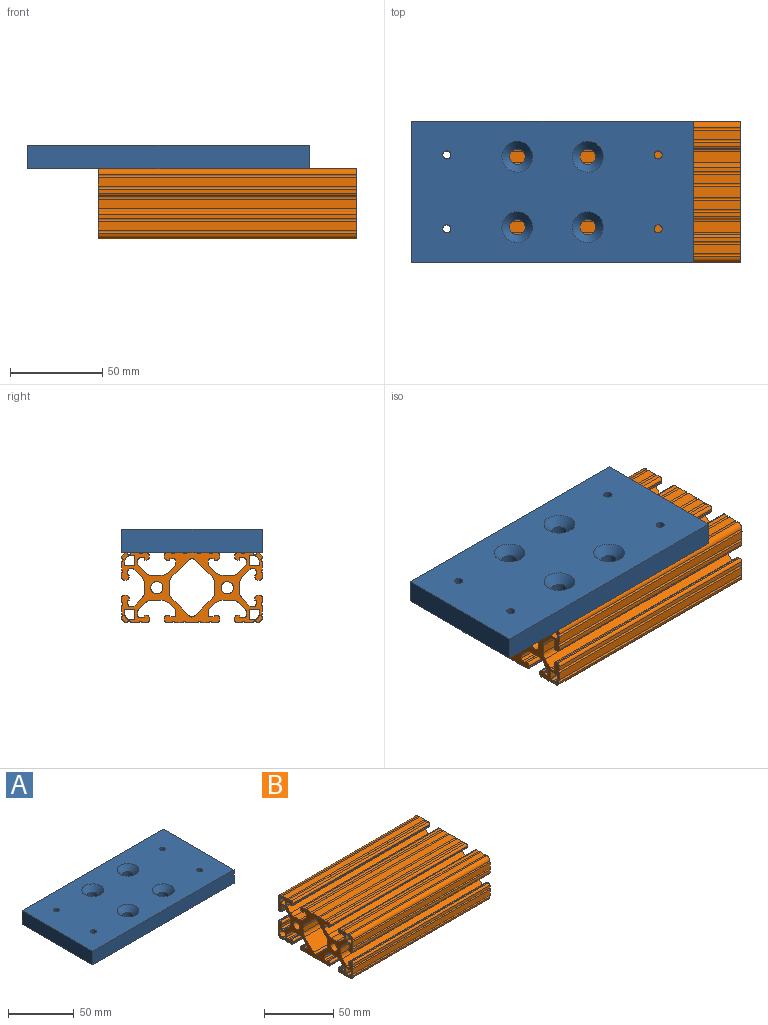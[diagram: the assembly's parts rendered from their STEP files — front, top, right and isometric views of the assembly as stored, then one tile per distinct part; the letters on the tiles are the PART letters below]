
ASSEMBLY  parts=2 mates=2
PART A: 22 faces, bbox 152.4x76.2x12.7 mm
  f0: plane 76.2x12.7mm, normal (1,0,0), area 967.7mm2, adj f1,f3,f4,f5
  f1: plane 152.4x12.7mm, normal (0,1,0), area 1935.5mm2, adj f0,f2,f4,f5
  f2: plane 76.2x12.7mm, normal (-1,0,0), area 967.7mm2, adj f1,f3,f4,f5
  f3: plane 152.4x12.7mm, normal (0,-1,0), area 1935.5mm2, adj f0,f2,f4,f5
  f4: plane 152.4x76.2mm, normal (0,0,1), area 10679.8mm2, adj f0,f1,f2,f3,f7,f9,f11,f13
  f5: plane 152.4x76.2mm, normal (0,0,-1), area 11137.3mm2, adj f0,f1,f2,f3,f6,f8,f10,f12
  f6: cylinder r=4.22mm len=8.43mm, axis (0,0,1), area 211.1mm2, adj f5,f7
  f7: cone r=4.22mm half-angle=41deg, axis (0,0,1), area 247.2mm2, adj f4,f6
  f8: cylinder r=4.22mm len=8.43mm, axis (0,0,1), area 211.1mm2, adj f5,f9
  f9: cone r=4.22mm half-angle=41deg, axis (0,0,1), area 247.2mm2, adj f4,f8
  f10: cylinder r=4.22mm len=8.43mm, axis (0,0,1), area 211.1mm2, adj f5,f11
  f11: cone r=4.22mm half-angle=41deg, axis (0,0,1), area 247.2mm2, adj f4,f10
  f12: cylinder r=4.22mm len=8.43mm, axis (0,0,1), area 211.1mm2, adj f5,f13
  f13: cone r=4.22mm half-angle=41deg, axis (0,0,1), area 247.2mm2, adj f4,f12
  f14: cylinder r=2.2mm len=10.42mm, axis (0,0,-1), area 144mm2, adj f4,f15
  f15: cone r=2.2mm half-angle=45deg, axis (0,0,-1), area 67.7mm2, adj f5,f14
  f16: cylinder r=2.2mm len=10.42mm, axis (0,0,-1), area 144mm2, adj f4,f17
  f17: cone r=2.2mm half-angle=45deg, axis (0,0,-1), area 67.7mm2, adj f5,f16
  f18: cylinder r=2.2mm len=10.42mm, axis (0,0,-1), area 144mm2, adj f4,f19
  f19: cone r=2.2mm half-angle=45deg, axis (0,0,-1), area 67.7mm2, adj f5,f18
  f20: cylinder r=2.2mm len=10.42mm, axis (0,0,-1), area 144mm2, adj f4,f21
  f21: cone r=2.2mm half-angle=45deg, axis (0,0,-1), area 67.7mm2, adj f5,f20
PART B: 266 faces, bbox 139.7x76.2x38.1 mm
  f0: cylinder r=0.76mm len=139.7mm, axis (-1,0,0), area 334.4mm2, adj f1,f263,f264,f265
  f1: plane 139.7x6.25mm, normal (0,0,1), area 872.8mm2, adj f0,f2,f264,f265
  f2: cylinder r=0.76mm len=139.7mm, axis (-1,0,0), area 334.4mm2, adj f1,f3,f264,f265
  f3: plane 139.7x4.83mm, normal (0,0,1), area 674.3mm2, adj f2,f4,f264,f265
  f4: cylinder r=0.76mm len=139.7mm, axis (-1,0,0), area 334.4mm2, adj f3,f5,f264,f265
  f5: plane 139.7x2.41mm, normal (0,0,1), area 337.1mm2, adj f4,f6,f264,f265
  f6: cylinder r=1.57mm len=139.7mm, axis (-1,0,0), area 345.6mm2, adj f5,f7,f264,f265
  f7: plane 139.7x0.91mm, normal (0,-1,0), area 127.7mm2, adj f6,f8,f264,f265
  f8: cylinder r=1.57mm len=139.7mm, axis (-1,0,0), area 345.6mm2, adj f7,f9,f264,f265
  f9: plane 139.7x0.94mm, normal (0,0,-1), area 131.4mm2, adj f8,f10,f264,f265
  f10: cylinder r=0.25mm len=139.7mm, axis (-1,0,0), area 55.7mm2, adj f9,f11,f264,f265
  f11: plane 139.7x0.26mm, normal (0,1,0), area 36.1mm2, adj f10,f12,f264,f265
  f12: cylinder r=0.25mm len=139.7mm, axis (-1,0,0), area 55.7mm2, adj f11,f13,f264,f265
  f13: plane 139.7x1.93mm, normal (0,0,-1), area 269.6mm2, adj f12,f14,f264,f265
  f14: cylinder r=1.27mm len=139.7mm, axis (-1,0,0), area 278.7mm2, adj f13,f15,f264,f265
  f15: plane 139.7x1.85mm, normal (0,-1,0), area 258.2mm2, adj f14,f16,f264,f265
  f16: cylinder r=0.89mm len=139.7mm, axis (-1,0,0), area 97.5mm2, adj f15,f17,f264,f265
  f17: plane 139.7x3.88mm, normal (0,-0.71,0.71), area 766.8mm2, adj f16,f18,f264,f265
  f18: cylinder r=4.67mm len=139.7mm, axis (-1,0,0), area 512.4mm2, adj f17,f19,f264,f265
  f19: plane 139.7x5.73mm, normal (0,0,1), area 800.9mm2, adj f18,f20,f264,f265
  f20: cylinder r=4.56mm len=139.7mm, axis (-1,0,0), area 499.9mm2, adj f19,f21,f264,f265
  f21: plane 139.7x3.8mm, normal (0,0.71,0.71), area 750.9mm2, adj f20,f22,f264,f265
  f22: cylinder r=1.28mm len=139.7mm, axis (-1,0,0), area 140.3mm2, adj f21,f23,f264,f265
  f23: plane 139.7x2.15mm, normal (0,1,0), area 300.9mm2, adj f22,f24,f264,f265
  f24: cylinder r=1.27mm len=139.7mm, axis (-1,0,0), area 278.7mm2, adj f23,f25,f264,f265
  f25: plane 139.7x1.93mm, normal (0,0,-1), area 269.6mm2, adj f24,f26,f264,f265
  f26: cylinder r=0.25mm len=139.7mm, axis (-1,0,0), area 55.7mm2, adj f25,f27,f264,f265
  f27: plane 139.7x0.73mm, normal (0,-1,0), area 101.4mm2, adj f26,f28,f264,f265
  f28: cylinder r=0.25mm len=139.7mm, axis (-1,0,0), area 55.7mm2, adj f27,f29,f264,f265
  f29: plane 139.7x0.94mm, normal (0,0,-1), area 131.4mm2, adj f28,f30,f264,f265
  f30: cylinder r=1.57mm len=139.7mm, axis (-1,0,0), area 345.6mm2, adj f29,f31,f264,f265
  f31: plane 139.7x0.89mm, normal (0,1,0), area 124.4mm2, adj f30,f32,f264,f265
  f32: cylinder r=1.6mm len=139.7mm, axis (-1,0,0), area 350.8mm2, adj f31,f33,f264,f265
  f33: plane 139.7x2.23mm, normal (0,0,1), area 312.1mm2, adj f32,f34,f264,f265
  f34: cylinder r=0.76mm len=139.7mm, axis (-1,0,0), area 334.4mm2, adj f33,f35,f264,f265
  f35: plane 139.7x4.93mm, normal (0,0,1), area 688.7mm2, adj f34,f36,f264,f265
  f36: cylinder r=0.81mm len=139.7mm, axis (-1,0,0), area 447.7mm2, adj f35,f37,f264,f265
  f37: cylinder r=3.17mm len=139.7mm, axis (-1,0,0), area 701.7mm2, adj f36,f38,f264,f265
  f38: cylinder r=0.76mm len=139.7mm, axis (-1,0,0), area 334.8mm2, adj f37,f39,f264,f265
  f39: plane 139.7x4.83mm, normal (0,-1,0), area 674.5mm2, adj f38,f40,f264,f265
  f40: cylinder r=0.76mm len=139.7mm, axis (-1,0,0), area 334.4mm2, adj f39,f41,f264,f265
  f41: plane 139.7x2.33mm, normal (0,-1,0), area 325.1mm2, adj f40,f42,f264,f265
  f42: cylinder r=1.53mm len=139.7mm, axis (-1,0,0), area 336.4mm2, adj f41,f43,f264,f265
  f43: plane 139.7x0.96mm, normal (0,0,-1), area 133.6mm2, adj f42,f44,f264,f265
  f44: cylinder r=1.57mm len=139.7mm, axis (-1,0,0), area 345.6mm2, adj f43,f45,f264,f265
  f45: plane 139.7x1.02mm, normal (0,1,0), area 142.2mm2, adj f44,f46,f264,f265
  f46: cylinder r=0.25mm len=139.7mm, axis (-1,0,0), area 55.7mm2, adj f45,f47,f264,f265
  f47: plane 139.7x0.1mm, normal (0,0,1), area 14.4mm2, adj f46,f48,f264,f265
  f48: cylinder r=0.25mm len=139.7mm, axis (-1,0,0), area 55.7mm2, adj f47,f49,f264,f265
  f49: plane 139.7x1.81mm, normal (0,1,0), area 253.5mm2, adj f48,f50,f264,f265
  f50: cylinder r=1.26mm len=139.7mm, axis (-1,0,0), area 277.4mm2, adj f49,f51,f264,f265
  f51: plane 139.7x1.35mm, normal (0,0,-1), area 188.5mm2, adj f50,f52,f264,f265
  f52: cylinder r=0.87mm len=139.7mm, axis (-1,0,0), area 95.3mm2, adj f51,f53,f264,f265
  f53: plane 139.7x4.22mm, normal (0,-0.71,-0.71), area 834mm2, adj f52,f54,f264,f265
  f54: cylinder r=4.75mm len=139.7mm, axis (-1,0,0), area 521.2mm2, adj f53,f55,f264,f265
  f55: plane 139.7x4.92mm, normal (0,-1,0), area 686.6mm2, adj f54,f56,f264,f265
  f56: cylinder r=4.75mm len=139.7mm, axis (-1,0,0), area 521.2mm2, adj f55,f57,f264,f265
  f57: plane 139.7x4.22mm, normal (0,-0.71,0.71), area 834mm2, adj f56,f58,f264,f265
  f58: cylinder r=0.87mm len=139.7mm, axis (-1,0,0), area 95.3mm2, adj f57,f59,f264,f265
  f59: plane 139.7x1.35mm, normal (0,0,1), area 188.5mm2, adj f58,f60,f264,f265
  f60: cylinder r=1.26mm len=139.7mm, axis (-1,0,0), area 277.4mm2, adj f59,f61,f264,f265
  f61: plane 139.7x1.81mm, normal (0,1,0), area 253.5mm2, adj f60,f62,f264,f265
  f62: cylinder r=0.25mm len=139.7mm, axis (-1,0,0), area 55.7mm2, adj f61,f63,f264,f265
  f63: plane 139.7x0.1mm, normal (0,0,-1), area 14.4mm2, adj f62,f64,f264,f265
  f64: cylinder r=0.25mm len=139.7mm, axis (-1,0,0), area 55.7mm2, adj f63,f65,f264,f265
  f65: plane 139.7x1.02mm, normal (0,1,0), area 142.2mm2, adj f64,f66,f264,f265
  f66: cylinder r=1.57mm len=139.7mm, axis (-1,0,0), area 345.6mm2, adj f65,f67,f264,f265
  f67: plane 139.7x0.96mm, normal (0,0,1), area 133.6mm2, adj f66,f68,f264,f265
  f68: cylinder r=1.53mm len=139.7mm, axis (-1,0,0), area 336.4mm2, adj f67,f69,f264,f265
  f69: plane 139.7x2.33mm, normal (0,-1,0), area 325.1mm2, adj f68,f70,f264,f265
  f70: cylinder r=0.76mm len=139.7mm, axis (-1,0,0), area 334.4mm2, adj f69,f71,f264,f265
  f71: plane 139.7x4.83mm, normal (0,-1,0), area 674.5mm2, adj f70,f72,f264,f265
  f72: cylinder r=0.76mm len=139.7mm, axis (-1,0,0), area 334.8mm2, adj f71,f73,f264,f265
  f73: cylinder r=3.17mm len=139.7mm, axis (-1,0,0), area 701.7mm2, adj f72,f74,f264,f265
  f74: cylinder r=0.81mm len=139.7mm, axis (-1,0,0), area 447.7mm2, adj f73,f75,f264,f265
  f75: plane 139.7x4.93mm, normal (0,0,-1), area 688.7mm2, adj f74,f76,f264,f265
  f76: cylinder r=0.76mm len=139.7mm, axis (-1,0,0), area 334.4mm2, adj f75,f77,f264,f265
  f77: plane 139.7x2.23mm, normal (0,0,-1), area 312.1mm2, adj f76,f78,f264,f265
  f78: cylinder r=1.6mm len=139.7mm, axis (-1,0,0), area 350.8mm2, adj f77,f79,f264,f265
  f79: plane 139.7x0.89mm, normal (0,1,0), area 124.4mm2, adj f78,f80,f264,f265
  f80: cylinder r=1.57mm len=139.7mm, axis (-1,0,0), area 345.6mm2, adj f79,f81,f264,f265
  f81: plane 139.7x0.94mm, normal (0,0,1), area 131.4mm2, adj f80,f82,f264,f265
  f82: cylinder r=0.25mm len=139.7mm, axis (-1,0,0), area 55.7mm2, adj f81,f83,f264,f265
  f83: plane 139.7x0.73mm, normal (0,-1,0), area 101.4mm2, adj f82,f84,f264,f265
  f84: cylinder r=0.25mm len=139.7mm, axis (-1,0,0), area 55.7mm2, adj f83,f85,f264,f265
  f85: plane 139.7x1.93mm, normal (0,0,1), area 269.6mm2, adj f84,f86,f264,f265
  f86: cylinder r=1.27mm len=139.7mm, axis (-1,0,0), area 278.7mm2, adj f85,f87,f264,f265
  f87: plane 139.7x2.15mm, normal (0,1,0), area 300.9mm2, adj f86,f88,f264,f265
  f88: cylinder r=1.28mm len=139.7mm, axis (-1,0,0), area 140.3mm2, adj f87,f89,f264,f265
  f89: plane 139.7x3.8mm, normal (0,0.71,-0.71), area 750.9mm2, adj f88,f90,f264,f265
  f90: cylinder r=4.56mm len=139.7mm, axis (-1,0,0), area 499.9mm2, adj f89,f91,f264,f265
  f91: plane 139.7x5.73mm, normal (0,0,-1), area 800.9mm2, adj f90,f92,f264,f265
  f92: cylinder r=4.67mm len=139.7mm, axis (-1,0,0), area 512.4mm2, adj f91,f93,f264,f265
  f93: plane 139.7x3.88mm, normal (0,-0.71,-0.71), area 766.8mm2, adj f92,f94,f264,f265
  f94: cylinder r=0.89mm len=139.7mm, axis (-1,0,0), area 97.5mm2, adj f93,f95,f264,f265
  f95: plane 139.7x1.85mm, normal (0,-1,0), area 258.2mm2, adj f94,f96,f264,f265
  f96: cylinder r=1.27mm len=139.7mm, axis (-1,0,0), area 278.7mm2, adj f95,f97,f264,f265
  f97: plane 139.7x1.93mm, normal (0,0,1), area 269.6mm2, adj f96,f98,f264,f265
  f98: cylinder r=0.25mm len=139.7mm, axis (-1,0,0), area 55.7mm2, adj f97,f99,f264,f265
  f99: plane 139.7x0.26mm, normal (0,1,0), area 36.1mm2, adj f98,f100,f264,f265
  f100: cylinder r=0.25mm len=139.7mm, axis (-1,0,0), area 55.7mm2, adj f99,f101,f264,f265
  f101: plane 139.7x0.94mm, normal (0,0,1), area 131.4mm2, adj f100,f102,f264,f265
  f102: cylinder r=1.57mm len=139.7mm, axis (-1,0,0), area 345.6mm2, adj f101,f103,f264,f265
  f103: plane 139.7x0.91mm, normal (0,-1,0), area 127.7mm2, adj f102,f104,f264,f265
  f104: cylinder r=1.57mm len=139.7mm, axis (-1,0,0), area 345.6mm2, adj f103,f105,f264,f265
  f105: plane 139.7x2.41mm, normal (0,0,-1), area 337.1mm2, adj f104,f106,f264,f265
  f106: cylinder r=0.76mm len=139.7mm, axis (-1,0,0), area 334.4mm2, adj f105,f107,f264,f265
  f107: plane 139.7x4.83mm, normal (0,0,-1), area 674.3mm2, adj f106,f108,f264,f265
  f108: cylinder r=0.76mm len=139.7mm, axis (-1,0,0), area 334.4mm2, adj f107,f109,f264,f265
  f109: plane 139.7x6.25mm, normal (0,0,-1), area 872.8mm2, adj f108,f110,f264,f265
  f110: cylinder r=0.76mm len=139.7mm, axis (-1,0,0), area 334.4mm2, adj f109,f111,f264,f265
  f111: plane 139.7x4.83mm, normal (0,0,-1), area 674.3mm2, adj f110,f112,f264,f265
  f112: cylinder r=0.76mm len=139.7mm, axis (-1,0,0), area 334.4mm2, adj f111,f113,f264,f265
  f113: plane 139.7x2.41mm, normal (0,0,-1), area 337.1mm2, adj f112,f114,f264,f265
  f114: cylinder r=1.57mm len=139.7mm, axis (-1,0,0), area 345.6mm2, adj f113,f115,f264,f265
  f115: plane 139.7x0.91mm, normal (0,1,0), area 127.7mm2, adj f114,f116,f264,f265
  f116: cylinder r=1.57mm len=139.7mm, axis (-1,0,0), area 345.6mm2, adj f115,f117,f264,f265
  f117: plane 139.7x0.94mm, normal (0,0,1), area 131.4mm2, adj f116,f118,f264,f265
  f118: cylinder r=0.25mm len=139.7mm, axis (-1,0,0), area 55.7mm2, adj f117,f119,f264,f265
  f119: plane 139.7x0.26mm, normal (0,-1,0), area 36.1mm2, adj f118,f120,f264,f265
  f120: cylinder r=0.25mm len=139.7mm, axis (-1,0,0), area 55.7mm2, adj f119,f121,f264,f265
  f121: plane 139.7x1.93mm, normal (0,0,1), area 269.6mm2, adj f120,f122,f264,f265
  f122: cylinder r=1.27mm len=139.7mm, axis (-1,0,0), area 278.7mm2, adj f121,f123,f264,f265
  f123: plane 139.7x1.85mm, normal (0,1,0), area 258.2mm2, adj f122,f124,f264,f265
  f124: cylinder r=0.89mm len=139.7mm, axis (-1,0,0), area 97.5mm2, adj f123,f125,f264,f265
  f125: plane 139.7x3.88mm, normal (0,0.71,-0.71), area 766.8mm2, adj f124,f126,f264,f265
  f126: cylinder r=4.67mm len=139.7mm, axis (-1,0,0), area 512.4mm2, adj f125,f127,f264,f265
  f127: plane 139.7x5.73mm, normal (0,0,-1), area 800.9mm2, adj f126,f128,f264,f265
  f128: cylinder r=4.56mm len=139.7mm, axis (-1,0,0), area 499.9mm2, adj f127,f129,f264,f265
  f129: plane 139.7x3.8mm, normal (0,-0.71,-0.71), area 750.9mm2, adj f128,f130,f264,f265
  f130: cylinder r=1.28mm len=139.7mm, axis (-1,0,0), area 140.3mm2, adj f129,f131,f264,f265
  f131: plane 139.7x2.15mm, normal (0,-1,0), area 300.9mm2, adj f130,f132,f264,f265
  f132: cylinder r=1.27mm len=139.7mm, axis (-1,0,0), area 278.7mm2, adj f131,f133,f264,f265
  f133: plane 139.7x1.93mm, normal (0,0,1), area 269.6mm2, adj f132,f134,f264,f265
  f134: cylinder r=0.25mm len=139.7mm, axis (-1,0,0), area 55.7mm2, adj f133,f135,f264,f265
  f135: plane 139.7x0.73mm, normal (0,1,0), area 101.4mm2, adj f134,f136,f264,f265
  f136: cylinder r=0.25mm len=139.7mm, axis (-1,0,0), area 55.7mm2, adj f135,f137,f264,f265
  f137: plane 139.7x0.94mm, normal (0,0,1), area 131.4mm2, adj f136,f138,f264,f265
  f138: cylinder r=1.57mm len=139.7mm, axis (-1,0,0), area 345.6mm2, adj f137,f139,f264,f265
  f139: plane 139.7x0.89mm, normal (0,-1,0), area 124.4mm2, adj f138,f140,f264,f265
  f140: cylinder r=1.6mm len=139.7mm, axis (-1,0,0), area 350.8mm2, adj f139,f141,f264,f265
  f141: plane 139.7x2.23mm, normal (0,0,-1), area 312.1mm2, adj f140,f142,f264,f265
  f142: cylinder r=0.76mm len=139.7mm, axis (-1,0,0), area 334.4mm2, adj f141,f143,f264,f265
  f143: plane 139.7x4.93mm, normal (0,0,-1), area 688.7mm2, adj f142,f144,f264,f265
  f144: cylinder r=0.81mm len=139.7mm, axis (-1,0,0), area 447.7mm2, adj f143,f145,f264,f265
  f145: cylinder r=3.17mm len=139.7mm, axis (-1,0,0), area 701.7mm2, adj f144,f146,f264,f265
  f146: cylinder r=0.76mm len=139.7mm, axis (-1,0,0), area 334.8mm2, adj f145,f147,f264,f265
  f147: plane 139.7x4.83mm, normal (0,1,0), area 674.5mm2, adj f146,f148,f264,f265
  f148: cylinder r=0.76mm len=139.7mm, axis (-1,0,0), area 334.4mm2, adj f147,f149,f264,f265
  f149: plane 139.7x2.33mm, normal (0,1,0), area 325.1mm2, adj f148,f150,f264,f265
  f150: cylinder r=1.53mm len=139.7mm, axis (-1,0,0), area 336.4mm2, adj f149,f151,f264,f265
  f151: plane 139.7x0.96mm, normal (0,0,1), area 133.6mm2, adj f150,f152,f264,f265
  f152: cylinder r=1.57mm len=139.7mm, axis (-1,0,0), area 345.6mm2, adj f151,f153,f264,f265
  f153: plane 139.7x1.02mm, normal (0,-1,0), area 142.2mm2, adj f152,f154,f264,f265
  f154: cylinder r=0.25mm len=139.7mm, axis (-1,0,0), area 55.7mm2, adj f153,f155,f264,f265
  f155: plane 139.7x0.1mm, normal (0,0,-1), area 14.4mm2, adj f154,f156,f264,f265
  f156: cylinder r=0.25mm len=139.7mm, axis (-1,0,0), area 55.7mm2, adj f155,f157,f264,f265
  f157: plane 139.7x1.81mm, normal (0,-1,0), area 253.5mm2, adj f156,f158,f264,f265
  f158: cylinder r=1.26mm len=139.7mm, axis (-1,0,0), area 277.4mm2, adj f157,f159,f264,f265
  f159: plane 139.7x1.35mm, normal (0,0,1), area 188.5mm2, adj f158,f160,f264,f265
  f160: cylinder r=0.87mm len=139.7mm, axis (-1,0,0), area 95.3mm2, adj f159,f161,f264,f265
  f161: plane 139.7x4.22mm, normal (0,0.71,0.71), area 834mm2, adj f160,f162,f264,f265
  f162: cylinder r=4.75mm len=139.7mm, axis (-1,0,0), area 521.2mm2, adj f161,f163,f264,f265
  f163: plane 139.7x4.92mm, normal (0,1,0), area 686.6mm2, adj f162,f164,f264,f265
  f164: cylinder r=4.75mm len=139.7mm, axis (-1,0,0), area 521.2mm2, adj f163,f165,f264,f265
  f165: plane 139.7x4.22mm, normal (0,0.71,-0.71), area 834mm2, adj f164,f166,f264,f265
  f166: cylinder r=0.87mm len=139.7mm, axis (-1,0,0), area 95.3mm2, adj f165,f167,f264,f265
  f167: plane 139.7x1.35mm, normal (0,0,-1), area 188.5mm2, adj f166,f168,f264,f265
  f168: cylinder r=1.26mm len=139.7mm, axis (-1,0,0), area 277.4mm2, adj f167,f169,f264,f265
  f169: plane 139.7x1.81mm, normal (0,-1,0), area 253.5mm2, adj f168,f170,f264,f265
  f170: cylinder r=0.25mm len=139.7mm, axis (-1,0,0), area 55.7mm2, adj f169,f171,f264,f265
  f171: plane 139.7x0.1mm, normal (0,0,1), area 14.4mm2, adj f170,f172,f264,f265
  f172: cylinder r=0.25mm len=139.7mm, axis (-1,0,0), area 55.7mm2, adj f171,f173,f264,f265
  f173: plane 139.7x1.02mm, normal (0,-1,0), area 142.2mm2, adj f172,f174,f264,f265
  f174: cylinder r=1.57mm len=139.7mm, axis (-1,0,0), area 345.6mm2, adj f173,f175,f264,f265
  f175: plane 139.7x0.96mm, normal (0,0,-1), area 133.6mm2, adj f174,f176,f264,f265
  f176: cylinder r=1.53mm len=139.7mm, axis (-1,0,0), area 336.4mm2, adj f175,f177,f264,f265
  f177: plane 139.7x2.33mm, normal (0,1,0), area 325.1mm2, adj f176,f178,f264,f265
  f178: cylinder r=0.76mm len=139.7mm, axis (-1,0,0), area 334.4mm2, adj f177,f179,f264,f265
  f179: plane 139.7x4.83mm, normal (0,1,0), area 674.5mm2, adj f178,f180,f264,f265
  f180: cylinder r=0.76mm len=139.7mm, axis (-1,0,0), area 334.8mm2, adj f179,f181,f264,f265
  f181: cylinder r=3.17mm len=139.7mm, axis (-1,0,0), area 701.7mm2, adj f180,f182,f264,f265
  f182: cylinder r=0.81mm len=139.7mm, axis (-1,0,0), area 447.7mm2, adj f181,f183,f264,f265
  f183: plane 139.7x4.93mm, normal (0,0,1), area 688.7mm2, adj f182,f184,f264,f265
  f184: cylinder r=0.76mm len=139.7mm, axis (-1,0,0), area 334.4mm2, adj f183,f185,f264,f265
  f185: plane 139.7x2.23mm, normal (0,0,1), area 312.1mm2, adj f184,f186,f264,f265
  f186: cylinder r=1.6mm len=139.7mm, axis (-1,0,0), area 350.8mm2, adj f185,f187,f264,f265
  f187: plane 139.7x0.89mm, normal (0,-1,0), area 124.4mm2, adj f186,f188,f264,f265
  f188: cylinder r=1.57mm len=139.7mm, axis (-1,0,0), area 345.6mm2, adj f187,f189,f264,f265
  f189: plane 139.7x0.94mm, normal (0,0,-1), area 131.4mm2, adj f188,f190,f264,f265
  f190: cylinder r=0.25mm len=139.7mm, axis (-1,0,0), area 55.7mm2, adj f189,f191,f264,f265
  f191: plane 139.7x0.73mm, normal (0,1,0), area 101.4mm2, adj f190,f192,f264,f265
  f192: cylinder r=0.25mm len=139.7mm, axis (-1,0,0), area 55.7mm2, adj f191,f193,f264,f265
  f193: plane 139.7x1.93mm, normal (0,0,-1), area 269.6mm2, adj f192,f194,f264,f265
  f194: cylinder r=1.27mm len=139.7mm, axis (-1,0,0), area 278.7mm2, adj f193,f195,f264,f265
  f195: plane 139.7x2.15mm, normal (0,-1,0), area 300.9mm2, adj f194,f196,f264,f265
  f196: cylinder r=1.28mm len=139.7mm, axis (-1,0,0), area 140.3mm2, adj f195,f197,f264,f265
  f197: plane 139.7x3.8mm, normal (0,-0.71,0.71), area 750.9mm2, adj f196,f198,f264,f265
  f198: cylinder r=4.56mm len=139.7mm, axis (-1,0,0), area 499.9mm2, adj f197,f199,f264,f265
  f199: plane 139.7x5.73mm, normal (0,0,1), area 800.9mm2, adj f198,f200,f264,f265
  f200: cylinder r=4.67mm len=139.7mm, axis (-1,0,0), area 512.4mm2, adj f199,f201,f264,f265
  f201: plane 139.7x3.88mm, normal (0,0.71,0.71), area 766.8mm2, adj f200,f202,f264,f265
  f202: cylinder r=0.89mm len=139.7mm, axis (-1,0,0), area 97.5mm2, adj f201,f203,f264,f265
  f203: plane 139.7x1.85mm, normal (0,1,0), area 258.2mm2, adj f202,f204,f264,f265
  f204: cylinder r=1.27mm len=139.7mm, axis (-1,0,0), area 278.7mm2, adj f203,f205,f264,f265
  f205: plane 139.7x1.93mm, normal (0,0,-1), area 269.6mm2, adj f204,f206,f264,f265
  f206: cylinder r=0.25mm len=139.7mm, axis (-1,0,0), area 55.7mm2, adj f205,f207,f264,f265
  f207: plane 139.7x0.26mm, normal (0,-1,0), area 36.1mm2, adj f206,f208,f264,f265
  f208: cylinder r=0.25mm len=139.7mm, axis (-1,0,0), area 55.7mm2, adj f207,f209,f264,f265
  f209: plane 139.7x0.94mm, normal (0,0,-1), area 131.4mm2, adj f208,f210,f264,f265
  f210: cylinder r=1.57mm len=139.7mm, axis (-1,0,0), area 345.6mm2, adj f209,f211,f264,f265
  f211: plane 139.7x0.91mm, normal (0,1,0), area 127.7mm2, adj f210,f212,f264,f265
  f212: cylinder r=1.57mm len=139.7mm, axis (-1,0,0), area 345.6mm2, adj f211,f213,f264,f265
  f213: plane 139.7x2.41mm, normal (0,0,1), area 337.1mm2, adj f212,f214,f264,f265
  f214: cylinder r=0.76mm len=139.7mm, axis (-1,0,0), area 334.4mm2, adj f213,f263,f264,f265
  f215: plane 139.7x2.34mm, normal (0,0,-1), area 326.5mm2, adj f216,f256,f264,f265
  f216: cylinder r=0.25mm len=139.7mm, axis (-1,0,0), area 55.7mm2, adj f215,f217,f264,f265
  f217: plane 139.7x4.88mm, normal (0,-1,0), area 681.3mm2, adj f216,f218,f264,f265
  f218: cylinder r=0.25mm len=139.7mm, axis (-1,0,0), area 55.7mm2, adj f217,f219,f264,f265
  f219: plane 139.7x4.88mm, normal (0,0,1), area 681.3mm2, adj f218,f220,f264,f265
  f220: cylinder r=0.25mm len=139.7mm, axis (-1,0,0), area 55.7mm2, adj f219,f221,f264,f265
  f221: plane 139.7x2.34mm, normal (0,1,0), area 326.5mm2, adj f220,f256,f264,f265
  f222: cylinder r=0.25mm len=139.7mm, axis (-1,0,0), area 55.7mm2, adj f223,f257,f264,f265
  f223: plane 139.7x4.88mm, normal (0,-1,0), area 681.3mm2, adj f222,f224,f264,f265
  f224: cylinder r=0.25mm len=139.7mm, axis (-1,0,0), area 55.7mm2, adj f223,f225,f264,f265
  f225: plane 139.7x2.34mm, normal (0,0,1), area 326.5mm2, adj f224,f226,f264,f265
  f226: cylinder r=2.79mm len=139.7mm, axis (-1,0,0), area 613.1mm2, adj f225,f227,f264,f265
  f227: plane 139.7x2.34mm, normal (0,1,0), area 326.5mm2, adj f226,f228,f264,f265
  f228: cylinder r=0.25mm len=139.7mm, axis (-1,0,0), area 55.7mm2, adj f227,f257,f264,f265
  f229: plane 139.7x9.12mm, normal (0,-0.71,0.71), area 1802mm2, adj f230,f258,f264,f265
  f230: cylinder r=3.22mm len=139.7mm, axis (-1,0,0), area 283.8mm2, adj f229,f231,f264,f265
  f231: cylinder r=3.22mm len=139.7mm, axis (-1,0,0), area 283.8mm2, adj f230,f232,f264,f265
  f232: plane 139.7x9.12mm, normal (0,0.71,0.71), area 1802mm2, adj f231,f233,f264,f265
  f233: cylinder r=4.75mm len=139.7mm, axis (-1,0,0), area 521.2mm2, adj f232,f234,f264,f265
  f234: plane 139.7x4.92mm, normal (0,1,0), area 686.6mm2, adj f233,f235,f264,f265
  f235: cylinder r=4.75mm len=139.7mm, axis (-1,0,0), area 521.2mm2, adj f234,f236,f264,f265
  f236: plane 139.7x9.12mm, normal (0,0.71,-0.71), area 1802mm2, adj f235,f237,f264,f265
  f237: cylinder r=3.22mm len=139.7mm, axis (-1,0,0), area 283.8mm2, adj f236,f238,f264,f265
  f238: cylinder r=3.22mm len=139.7mm, axis (-1,0,0), area 283.8mm2, adj f237,f239,f264,f265
  f239: plane 139.7x9.12mm, normal (0,-0.71,-0.71), area 1802mm2, adj f238,f240,f264,f265
  f240: cylinder r=4.75mm len=139.7mm, axis (-1,0,0), area 521.2mm2, adj f239,f241,f264,f265
  f241: plane 139.7x4.92mm, normal (0,-1,0), area 686.6mm2, adj f240,f258,f264,f265
  f242: cylinder r=2.79mm len=139.7mm, axis (-1,0,0), area 613.1mm2, adj f243,f259,f264,f265
  f243: plane 139.7x2.34mm, normal (0,0,1), area 326.5mm2, adj f242,f244,f264,f265
  f244: cylinder r=0.25mm len=139.7mm, axis (-1,0,0), area 55.7mm2, adj f243,f245,f264,f265
  f245: plane 139.7x4.88mm, normal (0,1,0), area 681.3mm2, adj f244,f246,f264,f265
  f246: cylinder r=0.25mm len=139.7mm, axis (-1,0,0), area 55.7mm2, adj f245,f247,f264,f265
  f247: plane 139.7x4.88mm, normal (0,0,-1), area 681.3mm2, adj f246,f248,f264,f265
  f248: cylinder r=0.25mm len=139.7mm, axis (-1,0,0), area 55.7mm2, adj f247,f259,f264,f265
  f249: cylinder r=0.25mm len=139.7mm, axis (-1,0,0), area 55.7mm2, adj f250,f260,f264,f265
  f250: plane 139.7x4.88mm, normal (0,1,0), area 681.3mm2, adj f249,f251,f264,f265
  f251: cylinder r=0.25mm len=139.7mm, axis (-1,0,0), area 55.7mm2, adj f250,f252,f264,f265
  f252: plane 139.7x2.34mm, normal (0,0,-1), area 326.5mm2, adj f251,f253,f264,f265
  f253: cylinder r=2.79mm len=139.7mm, axis (-1,0,0), area 613.1mm2, adj f252,f254,f264,f265
  f254: plane 139.7x2.34mm, normal (0,-1,0), area 326.5mm2, adj f253,f255,f264,f265
  f255: cylinder r=0.25mm len=139.7mm, axis (-1,0,0), area 55.7mm2, adj f254,f260,f264,f265
  f256: cylinder r=2.79mm len=139.7mm, axis (-1,0,0), area 613.1mm2, adj f215,f221,f264,f265
  f257: plane 139.7x4.88mm, normal (0,0,-1), area 681.3mm2, adj f222,f228,f264,f265
  f258: cylinder r=4.75mm len=139.7mm, axis (-1,0,0), area 521.2mm2, adj f229,f241,f264,f265
  f259: plane 139.7x2.34mm, normal (0,-1,0), area 326.5mm2, adj f242,f248,f264,f265
  f260: plane 139.7x4.88mm, normal (0,0,1), area 681.3mm2, adj f249,f255,f264,f265
  f261: cylinder r=3.33mm len=139.7mm, axis (-1,0,0), area 2920.7mm2, adj f264,f265
  f262: cylinder r=3.33mm len=139.7mm, axis (-1,0,0), area 2920.7mm2, adj f264,f265
  f263: plane 139.7x4.83mm, normal (0,0,1), area 674.3mm2, adj f0,f214,f264,f265
  f264: plane 76.2x38.1mm, normal (1,0,0), area 1112.2mm2, adj f0,f1,f2,f3,f4,f5,f6,f7
  f265: plane 76.2x38.1mm, normal (-1,0,0), area 1112.2mm2, adj f0,f1,f2,f3,f4,f5,f6,f7
PLACE A t=(65.05,-109.73,77.05)mm
PLACE B t=(96.8,-109.98,51.65)mm
MATE planar A.f5 <-> B.f1  axis (0,0,-1) through (65.05,-147.83,70.7)mm
MATE slider A.f5 <-> B.f1  axis (0,0,-1) through (65.05,-109.73,70.7)mm
